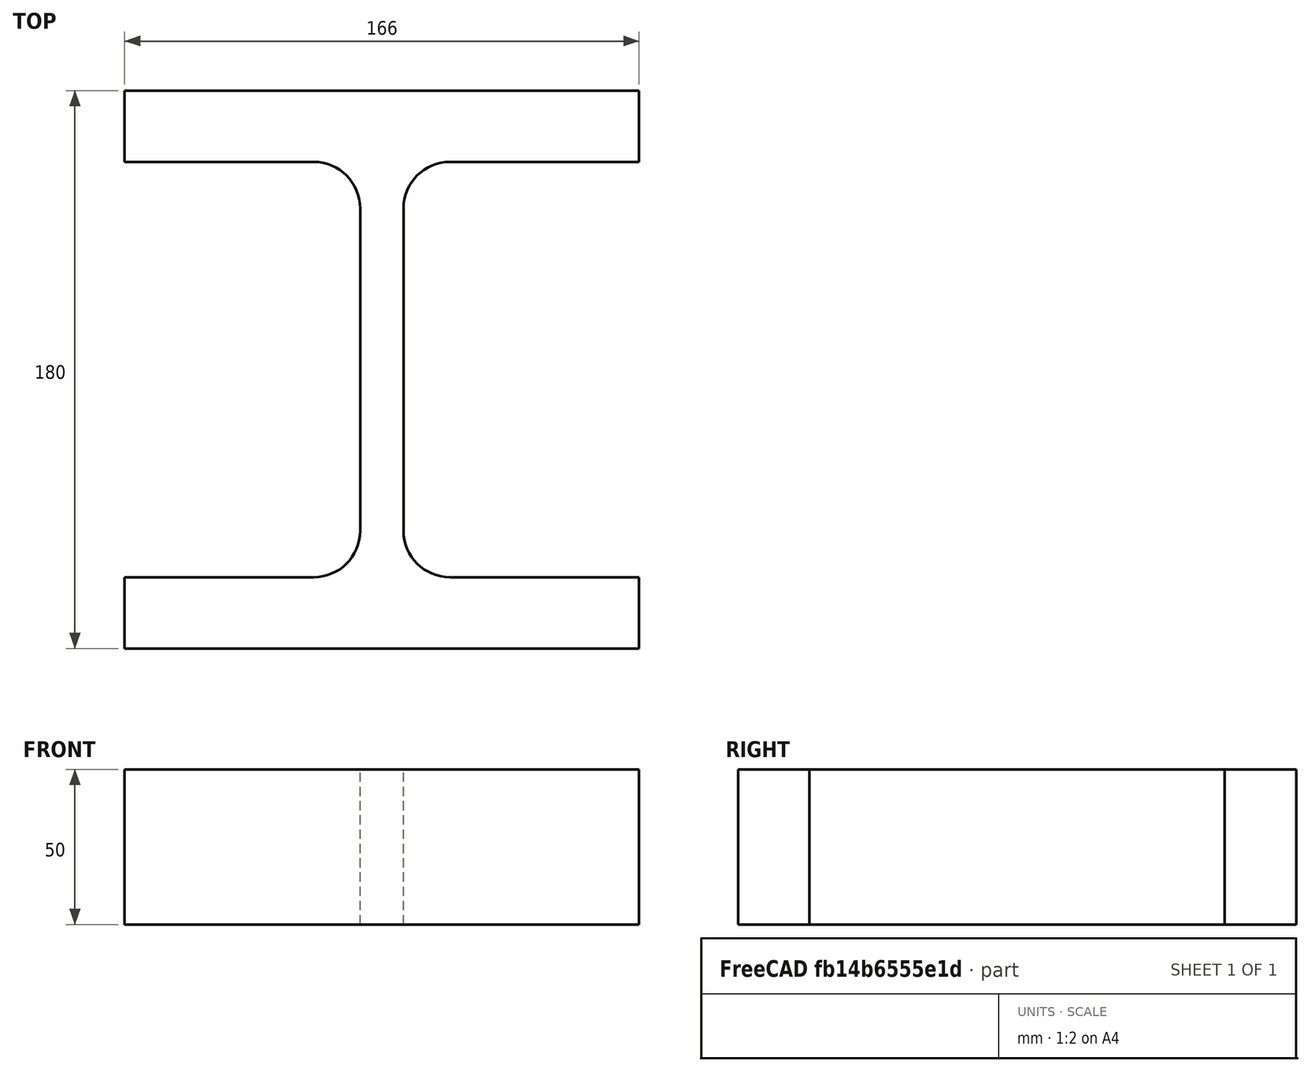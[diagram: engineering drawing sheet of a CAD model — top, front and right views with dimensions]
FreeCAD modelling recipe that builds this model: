
FCSTD DOCUMENT  (FreeCAD 0.15R4671 (Git))
Label: HE-M-Profile 160 DIN1025-4 S235JR
License: All rights reserved
LicenseURL: http://en.wikipedia.org/wiki/All_rights_reserved
objects: Sketcher::SketchObject×1, Part::Extrusion×1
note: 2 computed .brp shape members not serialized (recipe doc carries the construction recipe); baked Part::Feature solids carry a one-line shape summary decoded from their .brp

FEATURE [Sketcher::SketchObject] Sketch
  sketch-geometry (16):
    g0: LineSegment StartX=7 StartY=-52 StartZ=0 EndX=7 EndY=52 EndZ=0
    g1: LineSegment StartX=22 StartY=67 StartZ=0 EndX=83 EndY=67 EndZ=0
    g2: LineSegment StartX=83 StartY=67 StartZ=0 EndX=83 EndY=90 EndZ=0
    g3: LineSegment StartX=83 StartY=90 StartZ=0 EndX=-83 EndY=90 EndZ=0
    g4: LineSegment StartX=-83 StartY=90 StartZ=0 EndX=-83 EndY=67 EndZ=0
    g5: LineSegment StartX=-83 StartY=67 StartZ=0 EndX=-22 EndY=67 EndZ=0
    g6: LineSegment StartX=-7 StartY=52 StartZ=0 EndX=-7 EndY=-52 EndZ=0
    g7: LineSegment StartX=-22 StartY=-67 StartZ=0 EndX=-83 EndY=-67 EndZ=0
    g8: LineSegment StartX=-83 StartY=-67 StartZ=0 EndX=-83 EndY=-90 EndZ=0
    g9: LineSegment StartX=-83 StartY=-90 StartZ=0 EndX=83 EndY=-90 EndZ=0
    g10: LineSegment StartX=83 StartY=-90 StartZ=0 EndX=83 EndY=-67 EndZ=0
    g11: LineSegment StartX=83 StartY=-67 StartZ=0 EndX=22 EndY=-67 EndZ=0
    g12: ArcOfCircle CenterX=22 CenterY=52 CenterZ=0 NormalX=0 NormalY=0 NormalZ=1 Radius=15 StartAngle=1.5708 EndAngle=3.14159
    g13: ArcOfCircle CenterX=22 CenterY=-52 CenterZ=0 NormalX=0 NormalY=0 NormalZ=1 Radius=15 StartAngle=3.14159 EndAngle=4.71239
    g14: ArcOfCircle CenterX=-22 CenterY=52 CenterZ=0 NormalX=0 NormalY=0 NormalZ=1 Radius=15 StartAngle=0 EndAngle=1.5708
    g15: ArcOfCircle CenterX=-22 CenterY=-52 CenterZ=0 NormalX=0 NormalY=0 NormalZ=1 Radius=15 StartAngle=4.71239 EndAngle=6.28319
  constraints (42):
    c: Vertical(g0)
    c: Coincident(g2,g1)
    c: Vertical(g2)
    c: Coincident(g3,g2)
    c: Coincident(g4,g3)
    c: Vertical(g4)
    c: Coincident(g5,g4)
    c: Horizontal(g5)
    c: Vertical(g6)
    c: Horizontal(g7)
    c: Coincident(g8,g7)
    c: Vertical(g8)
    c: Coincident(g9,g8)
    c: Horizontal(g9)
    c: Coincident(g10,g9)
    c: Vertical(g10)
    c: Coincident(g11,g10)
    c: Horizontal(g11)
    c: Tangent(g1,g12) = 1.5708
    c: Tangent(g0,g12) = 1.5708
    c: Tangent(g0,g13) = 1.5708
    c: Tangent(g11,g13) = 1.5708
    c: Tangent(g5,g14) = 1.5708
    c: Tangent(g6,g14) = 1.5708
    c: Tangent(g6,g15) = 1.5708
    c: Tangent(g7,g15) = 1.5708
    c: Equal(g3,g9)
    c: Equal(g2,g4)
    c: Equal(g4,g8)
    c: Equal(g8,g10)
    c: Equal(g12,g14)
    c: Equal(g14,g15)
    c: Equal(g15,g13)
    c: Symmetric(g2,g3,g-2)
    c: Symmetric(g9,g8,g-2)
    c: Symmetric(g0,g6,g-2)
    c: Symmetric(g2,g9,g-1)
    c: DistanceY(g2,g9) = -180
    c: DistanceX(g3) = -166
    c: DistanceX(g0,g6) = -14
    c: DistanceY(g2) = 23
    c: Radius(g12) = 15
FEATURE [Part::Extrusion] Extrude  label="HE-M-Profile 160 DIN1025-4 S235JR"
  Base = -> Sketch
  Dir = (0,0,50)
  Solid = true
